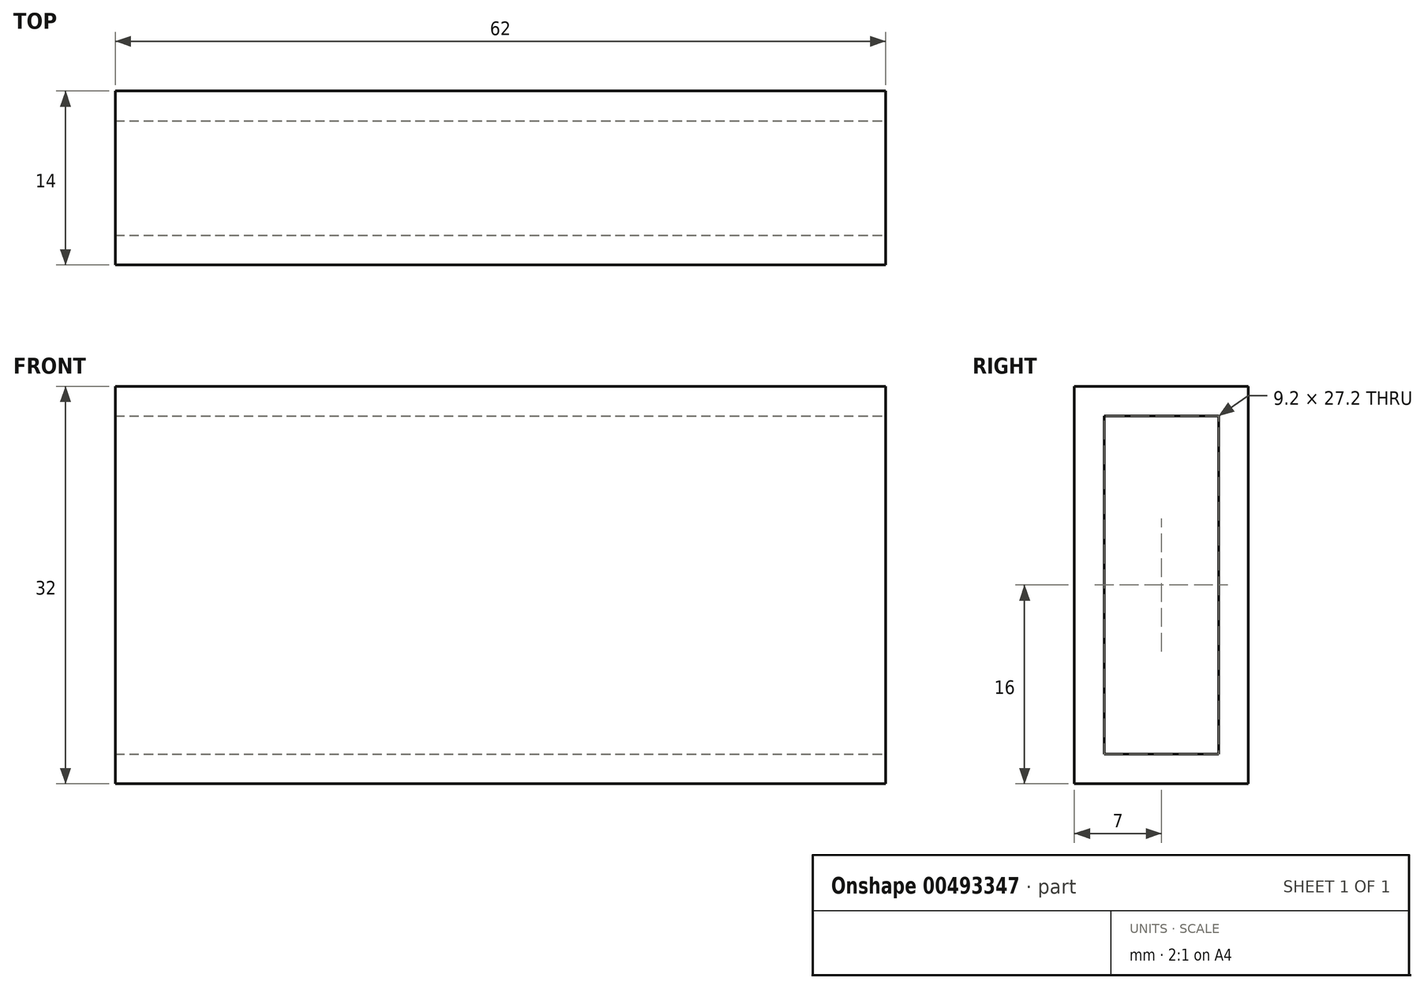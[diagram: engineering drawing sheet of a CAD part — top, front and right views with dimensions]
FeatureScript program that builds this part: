
annotation { "Feature Type Name" : "Feature", "Feature Type Description" : "" }
export const myFeature = defineFeature(function(context is Context, id is Id, definition is map)
    precondition{}
    {
        {
            var Q0;
            Q0=qCreatedBy(makeId("Front.planeOp"),FACE);
            var sketch = newSketch(context, id + "F0", { "sketchPlane" : qUnion([Q0])});
            skLineSegment(sketch, "E0.bottom", {"start": v(-31, 16) * mm, "end": v(31, 16) * mm});
            skLineSegment(sketch, "E0.top", {"start": v(-31, -16) * mm, "end": v(31, -16) * mm});
            skLineSegment(sketch, "E0.left", {"start": v(-31, 16) * mm, "end": v(-31, -16) * mm});
            skLineSegment(sketch, "E0.right", {"start": v(31, 16) * mm, "end": v(31, -16) * mm});
            skPoint(sketch, "E0.middle", {"position": v(0, 0) * mm});
            skSolve(sketch);
        }
        {
            var Q0;
            Q0 = qSketchRegion(id + "F0", true);
            extrude(context, id + "F1", {"entities" : qUnion([Q0]), "depth" : 14 * mm});
        }
        {
            var Q0;
            Q0=makeQuery(id+"F1.opExtrude","SWEPT_FACE",FACE,{"disambiguationData":[OSD([sQuery(id+"F0.wireOp",EDGE,"E0.right")])]});
            var Q1;
            Q1=makeQuery(id+"F1.opExtrude","SWEPT_FACE",FACE,{"disambiguationData":[OSD([sQuery(id+"F0.wireOp",EDGE,"E0.left")])]});
            shell(context, id + "F2", {"entities" : qUnion([Q0, Q1]), "thickness" : 2.4 * mm});
        }
    });
